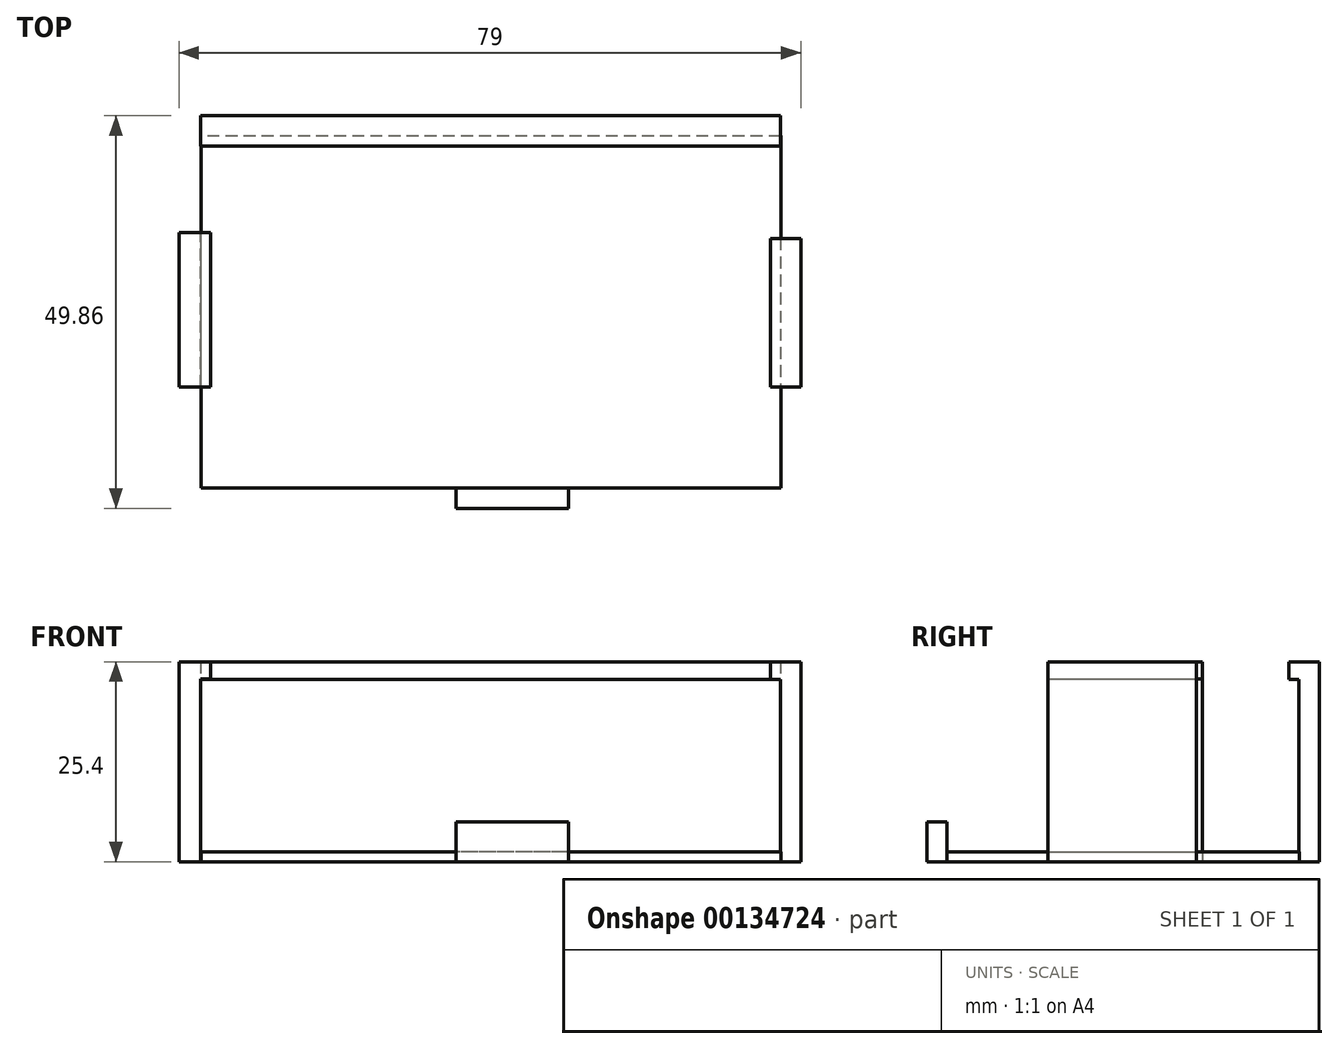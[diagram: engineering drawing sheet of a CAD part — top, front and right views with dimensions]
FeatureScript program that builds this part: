
annotation { "Feature Type Name" : "Feature", "Feature Type Description" : "" }
export const myFeature = defineFeature(function(context is Context, id is Id, definition is map)
    precondition{}
    {
        {
            var Q0;
            Q0=qCreatedBy(makeId("Top.planeOp"),FACE);
            var sketch = newSketch(context, id + "F0", { "sketchPlane" : qUnion([Q0])});
            skPoint(sketch, "E0.0", {"position": v(0, 0) * mm});
            skLineSegment(sketch, "E1", {"start": v(-39.51, 22.49) * mm, "end": v(34.15, 22.49) * mm});
            skLineSegment(sketch, "E2", {"start": v(34.15, 22.49) * mm, "end": v(34.15, -22.26) * mm});
            skLineSegment(sketch, "E3", {"start": v(34.15, -22.26) * mm, "end": v(-39.51, -22.26) * mm});
            skLineSegment(sketch, "E4", {"start": v(-39.51, -22.26) * mm, "end": v(-39.51, 22.49) * mm});
            skSolve(sketch);
        }
        {
            var Q0;
            Q0=makeQuery(id+"F0.imprint","IMPRINT",FACE,{"disambiguationData":[TD([[makeQuery(id+"F0.imprint","IMPRINT",EDGE,{"derivedFrom":sQuery(id+"F0.wireOp",EDGE,"E1")}),-1.0]])]});
            var sketch = newSketch(context, id + "F1", { "sketchPlane" : qUnion([Q0])});
            skLineSegment(sketch, "E5.bottom", {"start": v(-39.6, 22.45) * mm, "end": v(34.1, 22.45) * mm});
            skLineSegment(sketch, "E5.top", {"start": v(-39.6, 25.02) * mm, "end": v(34.1, 25.02) * mm});
            skLineSegment(sketch, "E5.left", {"start": v(-39.6, 22.45) * mm, "end": v(-39.6, 25.02) * mm});
            skLineSegment(sketch, "E5.right", {"start": v(34.1, 22.45) * mm, "end": v(34.1, 25.02) * mm});
            skLineSegment(sketch, "E6.bottom", {"start": v(34.1, 9.44) * mm, "end": v(36.66, 9.44) * mm});
            skLineSegment(sketch, "E6.top", {"start": v(34.1, -9.44) * mm, "end": v(36.66, -9.44) * mm});
            skLineSegment(sketch, "E6.left", {"start": v(34.1, 9.44) * mm, "end": v(34.1, -9.44) * mm});
            skLineSegment(sketch, "E6.right", {"start": v(36.66, 9.44) * mm, "end": v(36.66, -9.44) * mm});
            skLineSegment(sketch, "E7.bottom", {"start": v(-39.6, 10.17) * mm, "end": v(-42.34, 10.17) * mm});
            skLineSegment(sketch, "E7.top", {"start": v(-39.6, -9.44) * mm, "end": v(-42.34, -9.44) * mm});
            skLineSegment(sketch, "E7.left", {"start": v(-39.6, 10.17) * mm, "end": v(-39.6, -9.44) * mm});
            skLineSegment(sketch, "E7.right", {"start": v(-42.34, 10.17) * mm, "end": v(-42.34, -9.44) * mm});
            skSolve(sketch);
        }
        {
            var Q0;
            Q0=makeQuery(id+"F0.imprint","IMPRINT",FACE,{"disambiguationData":[TD([[makeQuery(id+"F0.imprint","IMPRINT",EDGE,{"derivedFrom":sQuery(id+"F0.wireOp",EDGE,"E1")}),-1.0]])]});
            var sketch = newSketch(context, id + "F2", { "sketchPlane" : qUnion([Q0])});
            skLineSegment(sketch, "E8.bottom", {"start": v(-7.15, -22.27) * mm, "end": v(7.15, -22.27) * mm});
            skLineSegment(sketch, "E8.top", {"start": v(-7.15, -24.84) * mm, "end": v(7.15, -24.84) * mm});
            skLineSegment(sketch, "E8.left", {"start": v(-7.15, -22.27) * mm, "end": v(-7.15, -24.84) * mm});
            skLineSegment(sketch, "E8.right", {"start": v(7.15, -22.27) * mm, "end": v(7.15, -24.84) * mm});
            skSolve(sketch);
        }
        {
            var Q0;
            Q0 = qSketchRegion(id + "F0", true);
            extrude(context, id + "F3", {"entities" : qUnion([Q0]), "depth" : 1.27 * mm});
        }
        {
            var Q0;
            Q0 = qSketchRegion(id + "F1", true);
            extrude(context, id + "F4", {"entities" : qUnion([Q0]), "operationType" : NewBodyOperationType.ADD, "depth" : 25.4 * mm});
        }
        {
            var Q0;
            Q0 = qSketchRegion(id + "F2", true);
            extrude(context, id + "F5", {"entities" : qUnion([Q0]), "depth" : 5.08 * mm});
        }
        {
            var Q0;
            Q0=makeQuery(id+"F4.opExtrude","SWEPT_FACE",FACE,{"disambiguationData":[OSD([sQuery(id+"F1.wireOp",EDGE,"E5.bottom")])]});
            var sketch = newSketch(context, id + "F6", { "sketchPlane" : qUnion([Q0])});
            skLineSegment(sketch, "E9", {"start": v(-39.6, 25.4) * mm, "end": v(34.1, 25.4) * mm});
            skLineSegment(sketch, "E10", {"start": v(34.1, 25.4) * mm, "end": v(34.1, 23.19) * mm});
            skLineSegment(sketch, "E11", {"start": v(34.1, 23.19) * mm, "end": v(-39.6, 23.19) * mm});
            skLineSegment(sketch, "E12", {"start": v(-39.6, 23.19) * mm, "end": v(-39.6, 25.4) * mm});
            skSolve(sketch);
        }
        {
            var Q0;
            Q0 = qSketchRegion(id + "F6", true);
            extrude(context, id + "F7", {"entities" : qUnion([Q0]), "operationType" : NewBodyOperationType.ADD, "depth" : 1.27 * mm});
        }
        {
            var Q0;
            Q0=makeQuery(id+"F4.opExtrude","SWEPT_FACE",FACE,{"disambiguationData":[OSD([sQuery(id+"F1.wireOp",EDGE,"E6.left")])]});
            var sketch = newSketch(context, id + "F8", { "sketchPlane" : qUnion([Q0])});
            skLineSegment(sketch, "E13", {"start": v(-9.44, 25.4) * mm, "end": v(-9.44, 23.18) * mm});
            skLineSegment(sketch, "E14", {"start": v(-9.44, 23.18) * mm, "end": v(9.44, 23.18) * mm});
            skLineSegment(sketch, "E15", {"start": v(9.44, 23.18) * mm, "end": v(9.44, 25.4) * mm});
            skLineSegment(sketch, "E16", {"start": v(9.44, 25.4) * mm, "end": v(-9.44, 25.4) * mm});
            skSolve(sketch);
        }
        {
            var Q0;
            Q0 = qSketchRegion(id + "F8", true);
            extrude(context, id + "F9", {"entities" : qUnion([Q0]), "operationType" : NewBodyOperationType.ADD, "depth" : 1.27 * mm});
        }
        {
            var Q0;
            Q0=makeQuery(id+"F4.opExtrude","SWEPT_FACE",FACE,{"disambiguationData":[OSD([sQuery(id+"F1.wireOp",EDGE,"E7.left")])]});
            var sketch = newSketch(context, id + "F10", { "sketchPlane" : qUnion([Q0])});
            skLineSegment(sketch, "E17", {"start": v(-9.44, 25.4) * mm, "end": v(-9.44, 23.2) * mm});
            skLineSegment(sketch, "E18", {"start": v(-9.44, 23.2) * mm, "end": v(10.17, 23.2) * mm});
            skLineSegment(sketch, "E19", {"start": v(10.17, 23.2) * mm, "end": v(10.17, 25.4) * mm});
            skLineSegment(sketch, "E20", {"start": v(10.17, 25.4) * mm, "end": v(-9.44, 25.4) * mm});
            skSolve(sketch);
        }
        {
            var Q0;
            Q0 = qSketchRegion(id + "F10", true);
            extrude(context, id + "F11", {"entities" : qUnion([Q0]), "operationType" : NewBodyOperationType.ADD, "depth" : 1.27 * mm});
        }
    });
